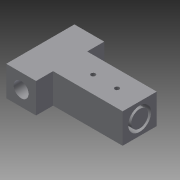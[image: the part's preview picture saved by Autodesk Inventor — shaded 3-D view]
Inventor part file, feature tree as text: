
AUTODESK INVENTOR PART (.ipt)
format: ipt  version: 2014 (Build 180170000, 170)  size: 132,608 bytes
history: native  units: mm
features: extrude x4, sketch x3, plane x1, other x1
ambient origin geometry x8: Origin, YZ Plane, XZ Plane, XY Plane, X Axis, Y Axis, Z Axis, Center Point
bodies: Solid1 (feature_tree)
feature tree (9):
  extrude  "Extrusion of Base"  Depth=50.8mm
  extrude  "Extrusion for 1 inch PVC"  Depth=25.4mm
  extrude  "Extrusion3"  Depth=34.0868mm
  plane  "Work Plane1"
  extrude  "Extrusion6"  Depth=25.3238mm
  other  "Base for Part"
  sketch  "Sketch for 1 inch PVC"  dims[d2=44.45mm d3=25.4mm]
  sketch  "Sketch of Base Hole"  dims[d4=44.45mm d5=0.0mm d6=34.0868mm d7=25.3238mm d8=114.55mm d9=0.0mm d10=22.3012mm d11=152.4mm d12=0.0mm d38=44.45mm d39=6.604mm d40=44.45mm d41=0.0mm d42=35.56mm d43=71.12mm]
  sketch  "Sketch9"  dims[d0=148.0mm d1=50.8mm]
